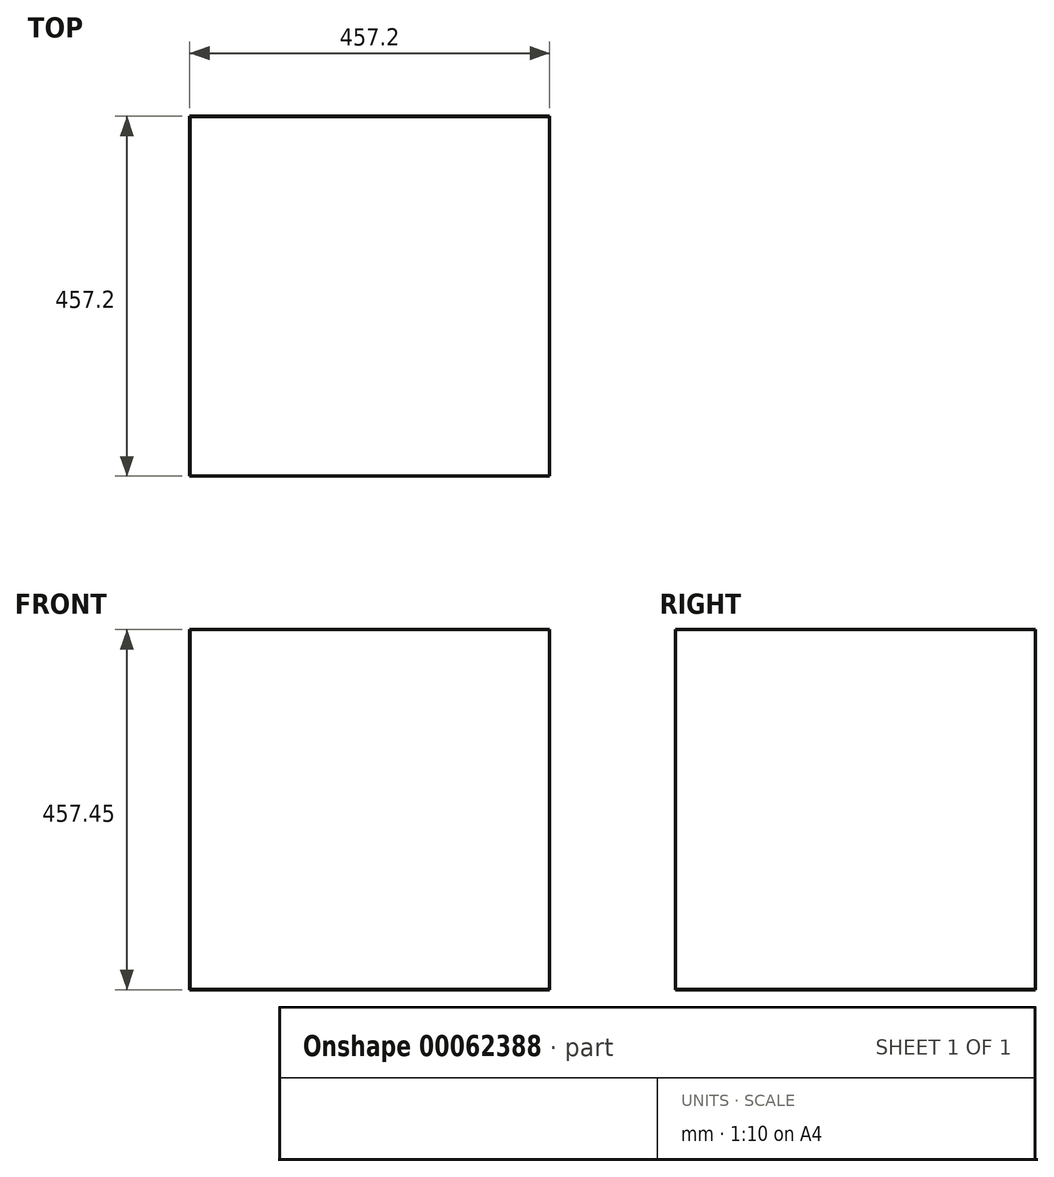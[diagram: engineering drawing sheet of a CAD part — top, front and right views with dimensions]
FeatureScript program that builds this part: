
annotation { "Feature Type Name" : "Feature", "Feature Type Description" : "" }
export const myFeature = defineFeature(function(context is Context, id is Id, definition is map)
    precondition{}
    {
        {
            var Q0;
            Q0=qCreatedBy(makeId("Top.planeOp"),FACE);
            var sketch = newSketch(context, id + "F0", { "sketchPlane" : qUnion([Q0])});
            skLineSegment(sketch, "E0.bottom", {"start": v(0, 0) * mm, "end": v(457.2, 0) * mm});
            skLineSegment(sketch, "E0.top", {"start": v(0, 457.2) * mm, "end": v(457.2, 457.2) * mm});
            skLineSegment(sketch, "E0.left", {"start": v(0, 0) * mm, "end": v(0, 457.2) * mm});
            skLineSegment(sketch, "E0.right", {"start": v(457.2, 0) * mm, "end": v(457.2, 457.2) * mm});
            skSolve(sketch);
        }
        {
            var Q0;
            Q0=makeQuery(id+"F0.imprint","IMPRINT",FACE,{"disambiguationData":[TD([[makeQuery(id+"F0.imprint","IMPRINT",EDGE,{"derivedFrom":sQuery(id+"F0.wireOp",EDGE,"E0.bottom")}),1.0]])]});
            extrude(context, id + "F1", {"entities" : qUnion([Q0]), "depth" : 0.25 * mm});
        }
        {
            var Q0;
            Q0=makeQuery(id+"F1.opExtrude","CAP_FACE",FACE,{"disambiguationData":[OSD([sQuery(id+"F0.wireOp",EDGE,"E0.bottom"),sQuery(id+"F0.wireOp",EDGE,"E0.top"),sQuery(id+"F0.wireOp",EDGE,"E0.left"),sQuery(id+"F0.wireOp",EDGE,"E0.right")])],"isStart":false});
            var sketch = newSketch(context, id + "F2", { "sketchPlane" : qUnion([Q0])});
            skLineSegment(sketch, "E1.bottom", {"start": v(0, 0) * mm, "end": v(0.25, 0) * mm});
            skLineSegment(sketch, "E1.top", {"start": v(0, 457.2) * mm, "end": v(0.25, 457.2) * mm});
            skLineSegment(sketch, "E1.left", {"start": v(0, 0) * mm, "end": v(0, 457.2) * mm});
            skLineSegment(sketch, "E1.right", {"start": v(0.25, 0) * mm, "end": v(0.25, 457.2) * mm});
            skLineSegment(sketch, "E2.bottom", {"start": v(0, 457.2) * mm, "end": v(457.2, 457.2) * mm});
            skLineSegment(sketch, "E2.top", {"start": v(0, 456.95) * mm, "end": v(457.2, 456.95) * mm});
            skLineSegment(sketch, "E2.left", {"start": v(0, 457.2) * mm, "end": v(0, 456.95) * mm});
            skLineSegment(sketch, "E2.right", {"start": v(457.2, 457.2) * mm, "end": v(457.2, 456.95) * mm});
            skSolve(sketch);
        }
        {
            var Q0;
            Q0=qSketchRegion(id+"F2",true);
            extrude(context, id + "F3", {"entities" : qUnion([Q0]), "operationType" : NewBodyOperationType.ADD, "depth" : 457.2 * mm});
        }
    });
